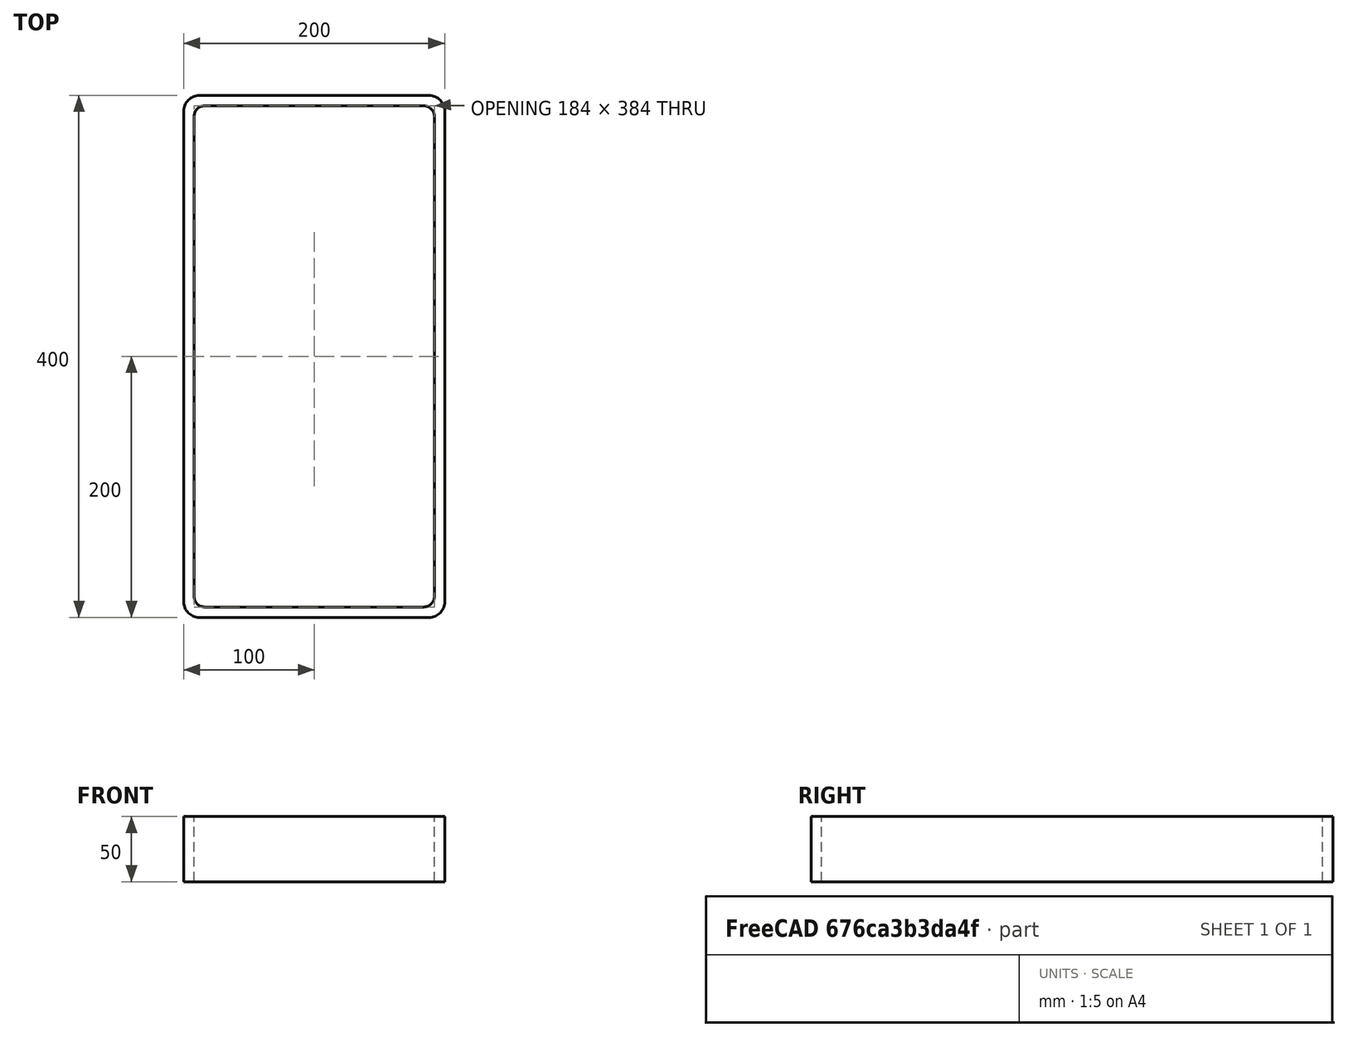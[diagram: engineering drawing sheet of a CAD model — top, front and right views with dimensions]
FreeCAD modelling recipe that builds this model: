
FCSTD DOCUMENT  (FreeCAD 0.15R4671 (Git))
Label: Rectangular hollow section 400x200x8 EN10219 S235JRH
License: All rights reserved
LicenseURL: http://en.wikipedia.org/wiki/All_rights_reserved
objects: Sketcher::SketchObject×1, Part::Extrusion×1
note: 2 computed .brp shape members not serialized (recipe doc carries the construction recipe); baked Part::Feature solids carry a one-line shape summary decoded from their .brp

FEATURE [Sketcher::SketchObject] Sketch
  sketch-geometry (16):
    g0: LineSegment StartX=-84 StartY=192 StartZ=0 EndX=84 EndY=192 EndZ=0
    g1: LineSegment StartX=92 StartY=184 StartZ=0 EndX=92 EndY=-184 EndZ=0
    g2: LineSegment StartX=84 StartY=-192 StartZ=0 EndX=-84 EndY=-192 EndZ=0
    g3: LineSegment StartX=-92 StartY=-184 StartZ=0 EndX=-92 EndY=184 EndZ=0
    g4: LineSegment StartX=-88 StartY=200 StartZ=0 EndX=88 EndY=200 EndZ=0
    g5: LineSegment StartX=100 StartY=188 StartZ=0 EndX=100 EndY=-188 EndZ=0
    g6: LineSegment StartX=88 StartY=-200 StartZ=0 EndX=-88 EndY=-200 EndZ=0
    g7: LineSegment StartX=-100 StartY=-188 StartZ=0 EndX=-100 EndY=188 EndZ=0
    g8: ArcOfCircle CenterX=-84 CenterY=184 CenterZ=0 NormalX=0 NormalY=0 NormalZ=1 Radius=8 StartAngle=1.5708 EndAngle=3.14159
    g9: ArcOfCircle CenterX=84 CenterY=184 CenterZ=0 NormalX=0 NormalY=0 NormalZ=1 Radius=8 StartAngle=0 EndAngle=1.5708
    g10: ArcOfCircle CenterX=84 CenterY=-184 CenterZ=0 NormalX=0 NormalY=0 NormalZ=1 Radius=8 StartAngle=4.71239 EndAngle=6.28319
    g11: ArcOfCircle CenterX=-84 CenterY=-184 CenterZ=0 NormalX=0 NormalY=0 NormalZ=1 Radius=8 StartAngle=3.14159 EndAngle=4.71239
    g12: ArcOfCircle CenterX=88 CenterY=188 CenterZ=0 NormalX=0 NormalY=0 NormalZ=1 Radius=12 StartAngle=0 EndAngle=1.5708
    g13: ArcOfCircle CenterX=88 CenterY=-188 CenterZ=0 NormalX=0 NormalY=0 NormalZ=1 Radius=12 StartAngle=4.71239 EndAngle=6.28319
    g14: ArcOfCircle CenterX=-88 CenterY=-188 CenterZ=0 NormalX=0 NormalY=0 NormalZ=1 Radius=12 StartAngle=3.14159 EndAngle=4.71239
    g15: ArcOfCircle CenterX=-88 CenterY=188 CenterZ=0 NormalX=0 NormalY=0 NormalZ=1 Radius=12 StartAngle=1.5708 EndAngle=3.14159
  constraints (36):
    c: Horizontal(g2)
    c: Vertical(g3)
    c: Horizontal(g6)
    c: Vertical(g7)
    c: Tangent(g3,g8) = 1.5708
    c: Tangent(g0,g8) = 1.5708
    c: Tangent(g0,g9) = 1.5708
    c: Tangent(g1,g9) = 1.5708
    c: Tangent(g1,g10) = 1.5708
    c: Tangent(g2,g10) = 1.5708
    c: Tangent(g2,g11) = 1.5708
    c: Tangent(g3,g11) = 1.5708
    c: Tangent(g4,g12) = 1.5708
    c: Tangent(g5,g12) = 1.5708
    c: Tangent(g5,g13) = 1.5708
    c: Tangent(g6,g13) = 1.5708
    c: Tangent(g6,g14) = 1.5708
    c: Tangent(g7,g14) = 1.5708
    c: Tangent(g7,g15) = 1.5708
    c: Tangent(g4,g15) = 1.5708
    c: Equal(g9,g8)
    c: Equal(g9,g11)
    c: Equal(g9,g10)
    c: Equal(g12,g15)
    c: Equal(g12,g14)
    c: Equal(g12,g13)
    c: Symmetric(g4,g6,g-1)
    c: Symmetric(g7,g5,g-2)
    c: DistanceY(g4,g6) = -400
    c: DistanceX(g7,g5) = 200
    c: Symmetric(g3,g1,g-2)
    c: Symmetric(g0,g2,g-1)
    c: DistanceY(g0,g4) = 8
    c: DistanceX(g5,g1) = -8
    c: Radius(g9) = 8
    c: Radius(g12) = 12
FEATURE [Part::Extrusion] Extrude  label="Rectangular hollow section 400x200x8 EN10219 S235JRH"
  Base = -> Sketch
  Dir = (0,0,50)
  Solid = true
